# Revit family: l-lego II 165
name_source: partatom
category: Осветительные приборы
revit_build: Autodesk Revit 2017 (Build: 20160225_1515(x64)
units: mm (PartAtom-declared; Revit-internal decimal feet)

## family parameters
Всегда вертикально = Да
Источник света = Да
На основе рабочей плоскости = Нет
Общий = Нет
При загрузке вырезать с полостями = Нет
Размер круглого соединителя = Использовать диаметр
Тип детали = Нормальный
Точка расчета площади = Нет

## types (8) — shared parameters
Изготовитель = LEDEL
Классификация нагрузок = Освещение
Комментарии к типоразмеру = Промышленные
Полная установленная мощность = 135 В·А
Светофильтр = 16777215
Смещение цветовой температуры при затухании лампы = <Нет>
Угол наклона = 90.00°

## per-type parameters (varying)
| type | Артикул | Файл фотометрической сетки |
| L-lego II 165 K15 5.0K | LII080 | L-lego 165-135-K15-5.0K-01.ies |
| L-lego II 165 G30 5.0K | LII068 | L-lego 165-135-G30-5.0K-01.ies |
| L-lego II 165 G60 5.0K | LII072 | L-lego 165-135-G60-5.0K-01.ies |
| L-lego II 165 D 5.0K | LII076 | L-lego 165-135-D-5.0K-01.ies |
| L-lego II 165 K15 4.0K | LII078 | L-lego 165-135-K15-5.0K-01.ies |
| L-lego II 165 G30 4.0K | LII066 | L-lego 165-135-G30-5.0K-01.ies |
| L-lego II 165 G60 4.0K | LII070 | L-lego 165-135-G60-5.0K-01.ies |
| L-lego II 165 D 4.0K | LII074 | L-lego 165-135-D-5.0K-01.ies |
